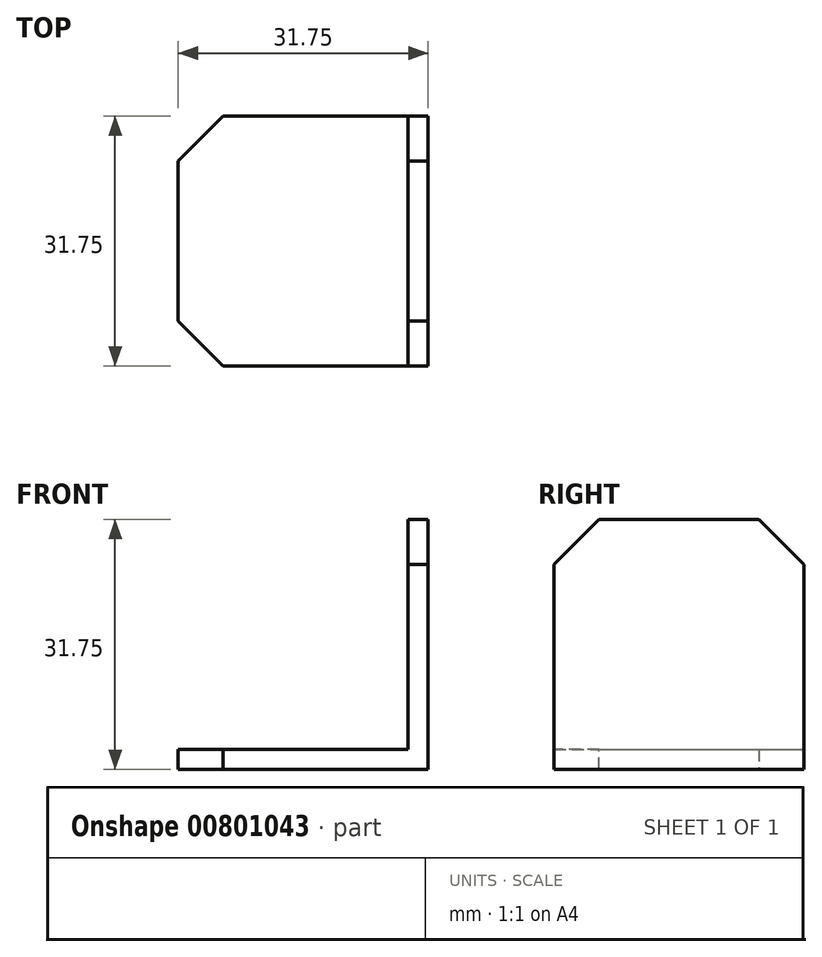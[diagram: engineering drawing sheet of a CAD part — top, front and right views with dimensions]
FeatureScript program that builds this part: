
annotation { "Feature Type Name" : "Feature", "Feature Type Description" : "" }
export const myFeature = defineFeature(function(context is Context, id is Id, definition is map)
    precondition{}
    {
        {
            var Q0;
            Q0=qCreatedBy(makeId("Top.planeOp"),FACE);
            var sketch = newSketch(context, id + "F0", { "sketchPlane" : qUnion([Q0])});
            skLineSegment(sketch, "E0.bottom", {"start": v(0, 0) * mm, "end": v(31.75, 0) * mm});
            skLineSegment(sketch, "E0.top", {"start": v(0, 31.75) * mm, "end": v(31.75, 31.75) * mm});
            skLineSegment(sketch, "E0.left", {"start": v(0, 0) * mm, "end": v(0, 31.75) * mm});
            skLineSegment(sketch, "E0.right", {"start": v(31.75, 0) * mm, "end": v(31.75, 31.75) * mm});
            skSolve(sketch);
        }
        {
            var Q0;
            Q0=makeQuery(id+"F0.imprint","IMPRINT",FACE,{"disambiguationData":[TD([[makeQuery(id+"F0.imprint","IMPRINT",EDGE,{"derivedFrom":sQuery(id+"F0.wireOp",EDGE,"E0.bottom")}),1.0]])]});
            extrude(context, id + "F1", {"entities" : qUnion([Q0]), "depth" : 31.75 * mm, "offsetDistance" : 25.4 * mm});
        }
        {
            var Q0;
            Q0=makeQuery(id+"F1.opExtrude","SWEPT_FACE",FACE,{"disambiguationData":[OSD([sQuery(id+"F0.wireOp",EDGE,"E0.top")])]});
            var sketch = newSketch(context, id + "F2", { "sketchPlane" : qUnion([Q0])});
            skLineSegment(sketch, "E1", {"start": v(-29.2, 31.75) * mm, "end": v(-29.2, 2.54) * mm});
            skLineSegment(sketch, "E2", {"start": v(0, 2.54) * mm, "end": v(-29.2, 2.54) * mm});
            skSolve(sketch);
        }
        {
            var Q0;
            {var subQ0=sQuery(id+"F2.wireOp",EDGE,"E1");Q0=makeQuery(id+"F2.imprint","IMPRINT",FACE,{"disambiguationData":[TD([[makeQuery(id+"F2.imprint","IMPRINT",EDGE,{"derivedFrom":subQ0}),1.0]])]});}
            extrude(context, id + "F3", {"entities" : qUnion([Q0]), "operationType" : NewBodyOperationType.REMOVE, "endBound" : BoundingType.UP_TO_NEXT, "oppositeDirection" : true, "depth" : 25.4 * mm, "offsetDistance" : 25.4 * mm});
        }
        {
            var Q0;
            Q0=makeQuery(id+"F1.opExtrude","CAP_EDGE",EDGE,{"disambiguationData":[OSD([sQuery(id+"F0.wireOp",EDGE,"E0.top")])],"isStart":false});
            var Q1;
            Q1=makeQuery(id+"F1.opExtrude","CAP_EDGE",EDGE,{"disambiguationData":[OSD([sQuery(id+"F0.wireOp",EDGE,"E0.bottom")])],"isStart":false});
            var Q2;
            Q2=makeQuery(id+"F1.opExtrude","SWEPT_EDGE",EDGE,{"disambiguationData":[OSD([sQuery(id+"F0.wireOp",EDGE,"E0.bottom"),sQuery(id+"F0.wireOp",EDGE,"E0.left")])]});
            var Q3;
            Q3=makeQuery(id+"F1.opExtrude","SWEPT_EDGE",EDGE,{"disambiguationData":[OSD([sQuery(id+"F0.wireOp",EDGE,"E0.top"),sQuery(id+"F0.wireOp",EDGE,"E0.left")])]});
            chamfer(context, id + "F4", {"entities" : qUnion([Q0, Q1, Q2, Q3]), "width" : 5.7 * mm, "tangentPropagation" : true});
        }
    });
